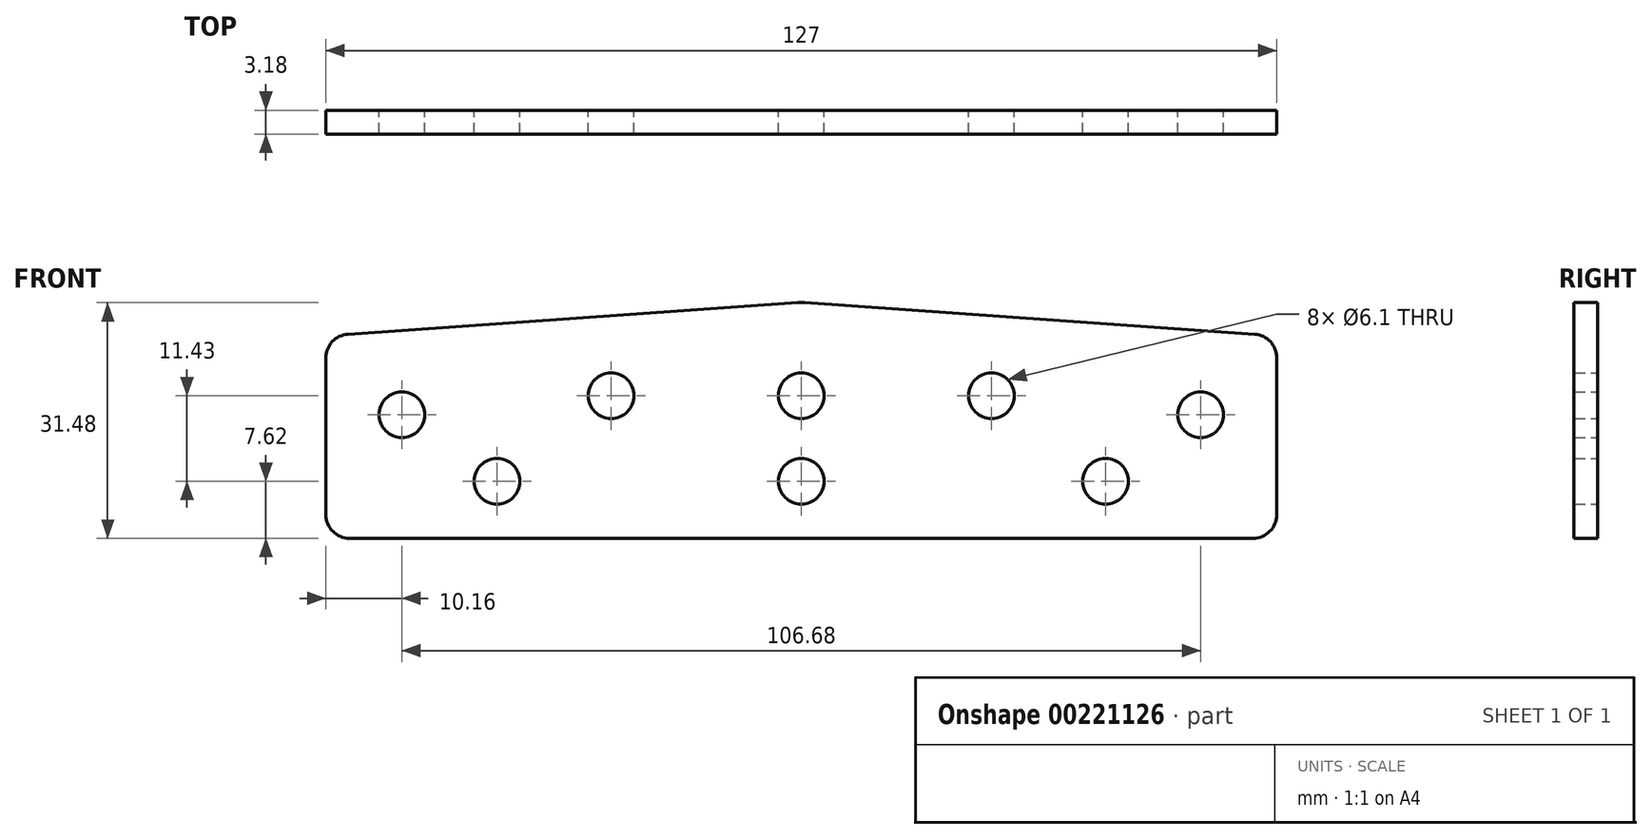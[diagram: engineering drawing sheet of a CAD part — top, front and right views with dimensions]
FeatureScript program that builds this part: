
annotation { "Feature Type Name" : "Feature", "Feature Type Description" : "" }
export const myFeature = defineFeature(function(context is Context, id is Id, definition is map)
    precondition{}
    {
        {
            var Q0;
            Q0=qCreatedBy(makeId("Front.planeOp"),FACE);
            var sketch = newSketch(context, id + "F0", { "sketchPlane" : qUnion([Q0])});
            skLineSegment(sketch, "E0.top", {"start": v(-60.33, 0) * mm, "end": v(60.33, 0) * mm});
            skLineSegment(sketch, "E0.right", {"start": v(63.5, 24.1) * mm, "end": v(63.5, 3.17) * mm});
            skLineSegment(sketch, "E1", {"start": v(-63.5, 24.1) * mm, "end": v(-63.5, 3.17) * mm});
            skPoint(sketch, "E2.visualSharp", {"position": v(63.5, 0) * mm});
            skPoint(sketch, "E3.visualSharp", {"position": v(-63.5, 0) * mm});
            skCircle(sketch, "E4", {"center": v(-40.64, 7.62) * mm, "radius": 3.05 * mm});
            skCircle(sketch, "E5", {"center": v(0, 7.62) * mm, "radius": 3.05 * mm});
            skCircle(sketch, "E6", {"center": v(53.34, 16.5) * mm, "radius": 3.05 * mm});
            skCircle(sketch, "E7", {"center": v(25.4, 19.05) * mm, "radius": 3.05 * mm});
            skCircle(sketch, "E8", {"center": v(0, 19.05) * mm, "radius": 3.05 * mm});
            skCircle(sketch, "E9", {"center": v(-25.4, 19.05) * mm, "radius": 3.05 * mm});
            skCircle(sketch, "E10", {"center": v(-53.34, 16.5) * mm, "radius": 3.05 * mm});
            skCircle(sketch, "E11", {"center": v(40.64, 7.62) * mm, "radius": 3.05 * mm});
            skArc(sketch, "E12.filletArc", {"start": v(-63.5, 3.17) * mm, "mid": v(-62.57, 0.93) * mm, "end": v(-60.33, 0) * mm});
            skArc(sketch, "E13.filletArc", {"start": v(60.33, 0) * mm, "mid": v(62.57, 0.93) * mm, "end": v(63.5, 3.17) * mm});
            skLineSegment(sketch, "E14", {"start": v(-60.55, 27.26) * mm, "end": v(-0.44, 31.46) * mm});
            skLineSegment(sketch, "E15", {"start": v(0.44, 31.46) * mm, "end": v(60.55, 27.26) * mm});
            skPoint(sketch, "E16.visualSharp", {"position": v(0, 31.5) * mm});
            skArc(sketch, "E16.filletArc", {"start": v(0.44, 31.46) * mm, "mid": v(0, 31.48) * mm, "end": v(-0.44, 31.46) * mm});
            skPoint(sketch, "E17.visualSharp", {"position": v(-63.5, 27.05) * mm});
            skArc(sketch, "E17.filletArc", {"start": v(-60.55, 27.26) * mm, "mid": v(-62.65, 26.26) * mm, "end": v(-63.5, 24.1) * mm});
            skPoint(sketch, "E18.visualSharp", {"position": v(63.5, 27.05) * mm});
            skArc(sketch, "E18.filletArc", {"start": v(63.5, 24.1) * mm, "mid": v(62.65, 26.26) * mm, "end": v(60.55, 27.26) * mm});
            skSolve(sketch);
        }
        {
            var Q0;
            Q0=makeQuery(id+"F0.imprint","IMPRINT",FACE,{"disambiguationData":[TD([[makeQuery(id+"F0.imprint","IMPRINT",EDGE,{"derivedFrom":sQuery(id+"F0.wireOp",EDGE,"E0.top")}),1.0]])]});
            extrude(context, id + "F1", {"entities" : qUnion([Q0]), "depth" : 3.17 * mm});
        }
    });
